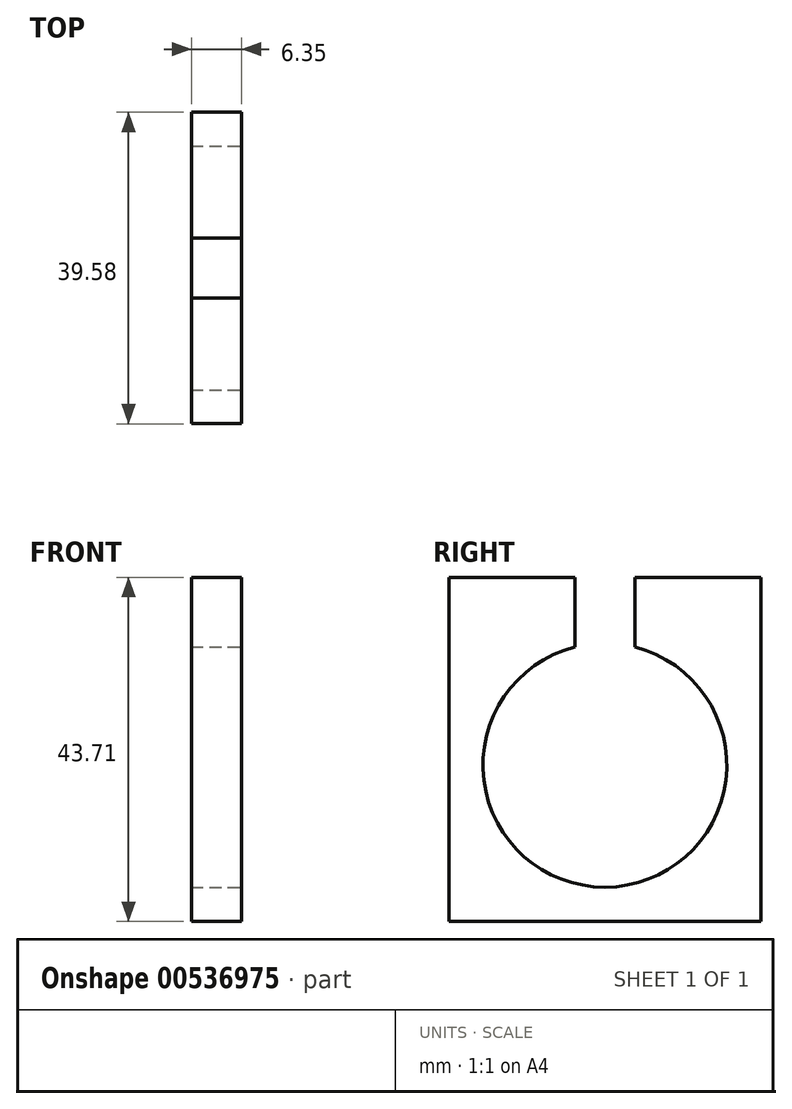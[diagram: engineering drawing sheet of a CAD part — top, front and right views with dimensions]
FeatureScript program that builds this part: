
annotation { "Feature Type Name" : "Feature", "Feature Type Description" : "" }
export const myFeature = defineFeature(function(context is Context, id is Id, definition is map)
    precondition{}
    {
        {
            var Q0;
            Q0=qCreatedBy(makeId("Right.planeOp"),FACE);
            var sketch = newSketch(context, id + "F0", { "sketchPlane" : qUnion([Q0])});
            skLineSegment(sketch, "E0.bottom", {"start": v(30.48, 31.75) * mm, "end": v(-30.48, 31.75) * mm});
            skLineSegment(sketch, "E0.top", {"start": v(30.48, -31.75) * mm, "end": v(-30.48, -31.75) * mm});
            skLineSegment(sketch, "E0.left", {"start": v(30.48, 31.75) * mm, "end": v(30.48, -31.75) * mm});
            skLineSegment(sketch, "E0.right", {"start": v(-30.48, 31.75) * mm, "end": v(-30.48, -31.75) * mm});
            skPoint(sketch, "E0.middle", {"position": v(0, 0) * mm});
            skSolve(sketch);
        }
        {
            var Q0;
            Q0 = qSketchRegion(id + "F0", true);
            extrude(context, id + "F1", {"entities" : qUnion([Q0]), "depth" : 6.35 * mm, "offsetDistance" : 25.4 * mm});
        }
        {
            var Q0;
            Q0=makeQuery(id+"F1.opExtrude","CAP_FACE",FACE,{"disambiguationData":[OSD([sQuery(id+"F0.wireOp",EDGE,"E0.bottom"),sQuery(id+"F0.wireOp",EDGE,"E0.top"),sQuery(id+"F0.wireOp",EDGE,"E0.left"),sQuery(id+"F0.wireOp",EDGE,"E0.right")])],"isStart":false});
            var sketch = newSketch(context, id + "F2", { "sketchPlane" : qUnion([Q0])});
            skCircle(sketch, "E1", {"center": v(0, 0) * mm, "radius": 15.5 * mm});
            skLineSegment(sketch, "E2.bottom", {"start": v(3.81, 15.02) * mm, "end": v(-3.8, 15.02) * mm});
            skLineSegment(sketch, "E2.top", {"start": v(3.8, 24.14) * mm, "end": v(-3.81, 24.14) * mm});
            skLineSegment(sketch, "E2.left", {"start": v(3.81, 15.02) * mm, "end": v(3.8, 24.14) * mm});
            skLineSegment(sketch, "E2.right", {"start": v(-3.8, 15.02) * mm, "end": v(-3.81, 24.14) * mm});
            skPoint(sketch, "E2.middle", {"position": v(0, 19.58) * mm});
            skSolve(sketch);
        }
        {
            var Q0;
            {var subQ0=sQuery(id+"F2.wireOp",EDGE,"E2.bottom");Q0=makeQuery(id+"F2.imprint","IMPRINT",FACE,{"disambiguationData":[TD([[makeQuery(id+"F2.imprint","IMPRINT",EDGE,{"derivedFrom":subQ0}),1.0]])]});}
            var Q1;
            Q1=makeQuery(id+"F2.imprint","IMPRINT",FACE,{"disambiguationData":[TD([[makeQuery(id+"F2.imprint","IMPRINT",EDGE,{"derivedFrom":sQuery(id+"F2.wireOp",EDGE,"E2.top")}),1.0]])]});
            extrude(context, id + "F3", {"entities" : qUnion([Q0, Q1]), "operationType" : NewBodyOperationType.REMOVE, "endBound" : BoundingType.THROUGH_ALL, "oppositeDirection" : true, "depth" : 25.4 * mm, "offsetDistance" : 25.4 * mm});
        }
        {
            var Q0;
            {var subQ0=sQuery(id+"F2.wireOp",EDGE,"E2.bottom");Q0=makeQuery(id+"F3.boolean.opBoolean","SPLIT",FACE,{"disambiguationData":[TD([makeQuery(id+"F3.opExtrude","SWEPT_FACE",FACE,{"disambiguationData":[OSD([subQ0])]})])],"derivedFrom":makeQuery(id+"F1.opExtrude","CAP_FACE",FACE,{"disambiguationData":[OSD([sQuery(id+"F0.wireOp",EDGE,"E0.bottom"),sQuery(id+"F0.wireOp",EDGE,"E0.top"),sQuery(id+"F0.wireOp",EDGE,"E0.left"),sQuery(id+"F0.wireOp",EDGE,"E0.right")])],"isStart":false})});}
            extrude(context, id + "F4", {"entities" : qUnion([Q0]), "operationType" : NewBodyOperationType.REMOVE, "endBound" : BoundingType.THROUGH_ALL, "oppositeDirection" : true, "depth" : 25.4 * mm, "offsetDistance" : 25.4 * mm});
        }
        {
            var Q0;
            {var subQ0=sQuery(id+"F0.wireOp",EDGE,"E0.left");var subQ5=sQuery(id+"F0.wireOp",EDGE,"E0.top");var subQ6=sQuery(id+"F0.wireOp",EDGE,"E0.right");var subQ7=sQuery(id+"F0.wireOp",EDGE,"E0.bottom");Q0=makeQuery(id+"F3.boolean.opBoolean","SPLIT",FACE,{"disambiguationData":[TD([makeQuery(id+"F1.opExtrude","SWEPT_FACE",FACE,{"disambiguationData":[OSD([subQ7])]})])],"derivedFrom":makeQuery(id+"F1.opExtrude","CAP_FACE",FACE,{"disambiguationData":[OSD([subQ7,subQ5,subQ0,subQ6])],"isStart":false})});}
            var sketch = newSketch(context, id + "F5", { "sketchPlane" : qUnion([Q0])});
            skLineSegment(sketch, "E3.bottom", {"start": v(-30.48, 31.75) * mm, "end": v(30.48, 31.75) * mm});
            skLineSegment(sketch, "E3.top", {"start": v(-30.48, 23.88) * mm, "end": v(30.48, 23.88) * mm});
            skLineSegment(sketch, "E3.left", {"start": v(-30.48, 31.75) * mm, "end": v(-30.48, 23.88) * mm});
            skLineSegment(sketch, "E3.right", {"start": v(30.48, 31.75) * mm, "end": v(30.48, 23.88) * mm});
            skSolve(sketch);
        }
        {
            var Q0;
            Q0=makeQuery(id+"F5.imprint","IMPRINT",FACE,{"disambiguationData":[TD([[makeQuery(id+"F5.imprint","IMPRINT",EDGE,{"derivedFrom":sQuery(id+"F5.wireOp",EDGE,"E3.bottom")}),1.0]])]});
            extrude(context, id + "F6", {"entities" : qUnion([Q0]), "operationType" : NewBodyOperationType.REMOVE, "endBound" : BoundingType.THROUGH_ALL, "oppositeDirection" : true, "depth" : 25.4 * mm, "offsetDistance" : 25.4 * mm});
        }
        {
            var Q0;
            {var subQ0=sQuery(id+"F0.wireOp",EDGE,"E0.left");var subQ5=sQuery(id+"F0.wireOp",EDGE,"E0.top");var subQ6=sQuery(id+"F0.wireOp",EDGE,"E0.right");var subQ7=sQuery(id+"F0.wireOp",EDGE,"E0.bottom");Q0=makeQuery(id+"F3.boolean.opBoolean","SPLIT",FACE,{"disambiguationData":[TD([makeQuery(id+"F1.opExtrude","SWEPT_FACE",FACE,{"disambiguationData":[OSD([subQ7])]})])],"derivedFrom":makeQuery(id+"F1.opExtrude","CAP_FACE",FACE,{"disambiguationData":[OSD([subQ7,subQ5,subQ0,subQ6])],"isStart":false})});}
            var sketch = newSketch(context, id + "F7", { "sketchPlane" : qUnion([Q0])});
            skLineSegment(sketch, "E4.bottom", {"start": v(-30.48, 23.88) * mm, "end": v(-19.78, 23.88) * mm});
            skLineSegment(sketch, "E4.top", {"start": v(-30.48, -31.75) * mm, "end": v(-19.78, -31.75) * mm});
            skLineSegment(sketch, "E4.left", {"start": v(-30.48, 23.88) * mm, "end": v(-30.48, -31.75) * mm});
            skLineSegment(sketch, "E4.right", {"start": v(-19.78, 23.88) * mm, "end": v(-19.78, -31.75) * mm});
            skLineSegment(sketch, "E5.bottom", {"start": v(30.48, 23.88) * mm, "end": v(19.8, 23.88) * mm});
            skLineSegment(sketch, "E5.top", {"start": v(30.48, -31.75) * mm, "end": v(19.8, -31.75) * mm});
            skLineSegment(sketch, "E5.left", {"start": v(30.48, 23.88) * mm, "end": v(30.48, -31.75) * mm});
            skLineSegment(sketch, "E5.right", {"start": v(19.8, 23.88) * mm, "end": v(19.8, -31.75) * mm});
            skLineSegment(sketch, "E6.bottom", {"start": v(-19.78, -31.75) * mm, "end": v(19.8, -31.75) * mm});
            skLineSegment(sketch, "E6.top", {"start": v(-19.78, -19.83) * mm, "end": v(19.8, -19.83) * mm});
            skLineSegment(sketch, "E6.left", {"start": v(-19.78, -31.75) * mm, "end": v(-19.78, -19.83) * mm});
            skLineSegment(sketch, "E6.right", {"start": v(19.8, -31.75) * mm, "end": v(19.8, -19.83) * mm});
            skSolve(sketch);
        }
        {
            var Q0;
            Q0=makeQuery(id+"F7.imprint","IMPRINT",FACE,{"disambiguationData":[TD([[makeQuery(id+"F7.imprint","IMPRINT",EDGE,{"derivedFrom":sQuery(id+"F7.wireOp",EDGE,"E4.bottom")}),-1.0]])]});
            var Q1;
            Q1=makeQuery(id+"F7.imprint","IMPRINT",FACE,{"disambiguationData":[TD([[makeQuery(id+"F7.imprint","IMPRINT",EDGE,{"derivedFrom":sQuery(id+"F7.wireOp",EDGE,"E5.bottom")}),-1.0]])]});
            var Q2;
            Q2=makeQuery(id+"F7.imprint","IMPRINT",FACE,{"disambiguationData":[TD([[makeQuery(id+"F7.imprint","IMPRINT",EDGE,{"derivedFrom":sQuery(id+"F7.wireOp",EDGE,"E6.bottom")}),-1.0]])]});
            extrude(context, id + "F8", {"entities" : qUnion([Q0, Q1, Q2]), "operationType" : NewBodyOperationType.REMOVE, "endBound" : BoundingType.THROUGH_ALL, "oppositeDirection" : true, "depth" : 25.4 * mm, "offsetDistance" : 25.4 * mm});
        }
    });
